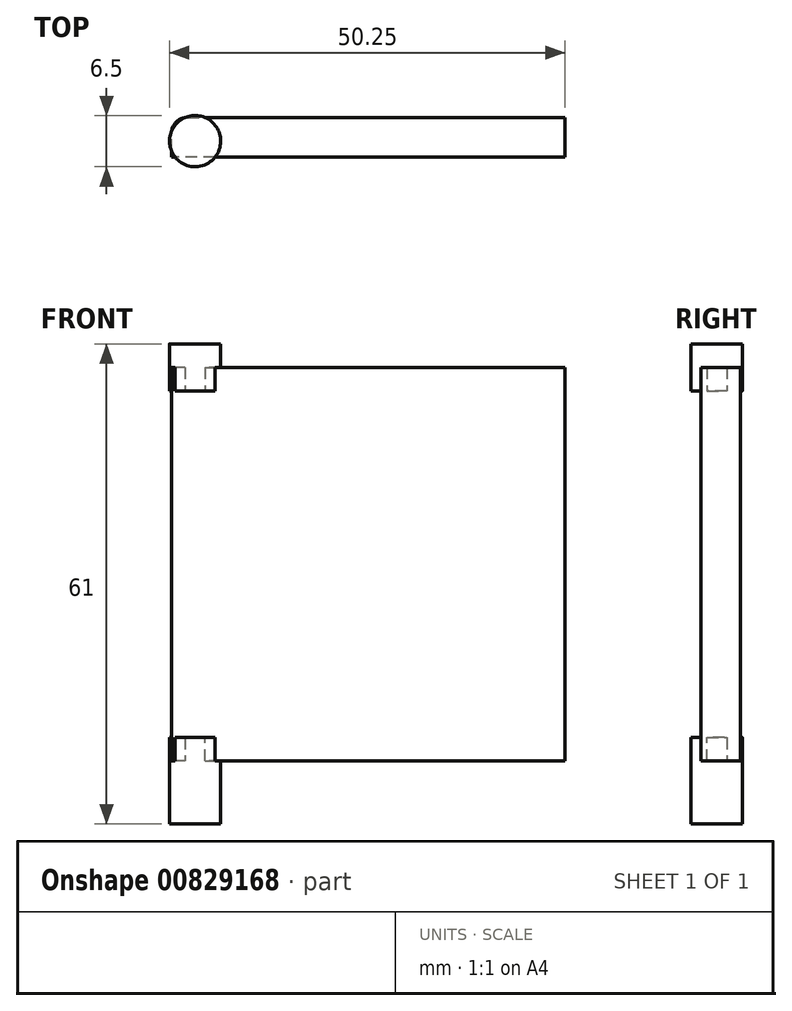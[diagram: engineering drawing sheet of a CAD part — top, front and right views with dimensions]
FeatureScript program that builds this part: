
annotation { "Feature Type Name" : "Feature", "Feature Type Description" : "" }
export const myFeature = defineFeature(function(context is Context, id is Id, definition is map)
    precondition{}
    {
        {
            var Q0;
            Q0=qCreatedBy(makeId("Front.planeOp"),FACE);
            var sketch = newSketch(context, id + "F0", { "sketchPlane" : qUnion([Q0])});
            skLineSegment(sketch, "E0.bottom", {"start": v(0, 0) * mm, "end": v(50, 0) * mm});
            skLineSegment(sketch, "E0.top", {"start": v(0, 50) * mm, "end": v(50, 50) * mm});
            skLineSegment(sketch, "E0.left", {"start": v(0, 0) * mm, "end": v(0, 50) * mm});
            skLineSegment(sketch, "E0.right", {"start": v(50, 0) * mm, "end": v(50, 50) * mm});
            skSolve(sketch);
        }
        {
            var Q0;
            Q0 = qSketchRegion(id + "F0", true);
            extrude(context, id + "F1", {"entities" : qUnion([Q0]), "depth" : 5 * mm, "offsetDistance" : 25 * mm});
        }
        {
            var Q0;
            Q0=makeQuery(id+"F1.opExtrude","SWEPT_FACE",FACE,{"disambiguationData":[OSD([sQuery(id+"F0.wireOp",EDGE,"E0.bottom")])]});
            var sketch = newSketch(context, id + "F2", { "sketchPlane" : qUnion([Q0])});
            skCircle(sketch, "E1", {"center": v(3, 3) * mm, "radius": 3.25 * mm});
            skSolve(sketch);
        }
        {
            var Q0;
            Q0 = qSketchRegion(id + "F2", true);
            extrude(context, id + "F3", {"entities" : qUnion([Q0]), "operationType" : NewBodyOperationType.ADD, "depth" : 8 * mm, "offsetDistance" : 25 * mm, "hasSecondDirection" : true, "secondDirectionOppositeDirection" : true, "secondDirectionDepth" : 3 * mm});
        }
        {
            var Q0;
            Q0=makeQuery(id+"F1.opExtrude","SWEPT_FACE",FACE,{"disambiguationData":[OSD([sQuery(id+"F0.wireOp",EDGE,"E0.top")])]});
            var sketch = newSketch(context, id + "F4", { "sketchPlane" : qUnion([Q0])});
            skCircle(sketch, "E2", {"center": v(3, -3) * mm, "radius": 3.25 * mm});
            skSolve(sketch);
        }
        {
            var Q0;
            Q0 = qSketchRegion(id + "F4", true);
            extrude(context, id + "F5", {"entities" : qUnion([Q0]), "operationType" : NewBodyOperationType.ADD, "depth" : 3 * mm, "offsetDistance" : 25 * mm, "hasSecondDirection" : true, "secondDirectionOppositeDirection" : true, "secondDirectionDepth" : 3 * mm});
        }
        {
            var Q0;
            Q0=makeQuery(id+"F1.opExtrude","CAP_EDGE",EDGE,{"disambiguationData":[OSD([sQuery(id+"F0.wireOp",EDGE,"E0.left")])],"isStart":true});
            fillet(context, id + "F6", {"entities" : qUnion([Q0]), "radius" : 2 * mm, "tangentPropagation" : true, "allowEdgeOverflow" : false});
        }
    });
